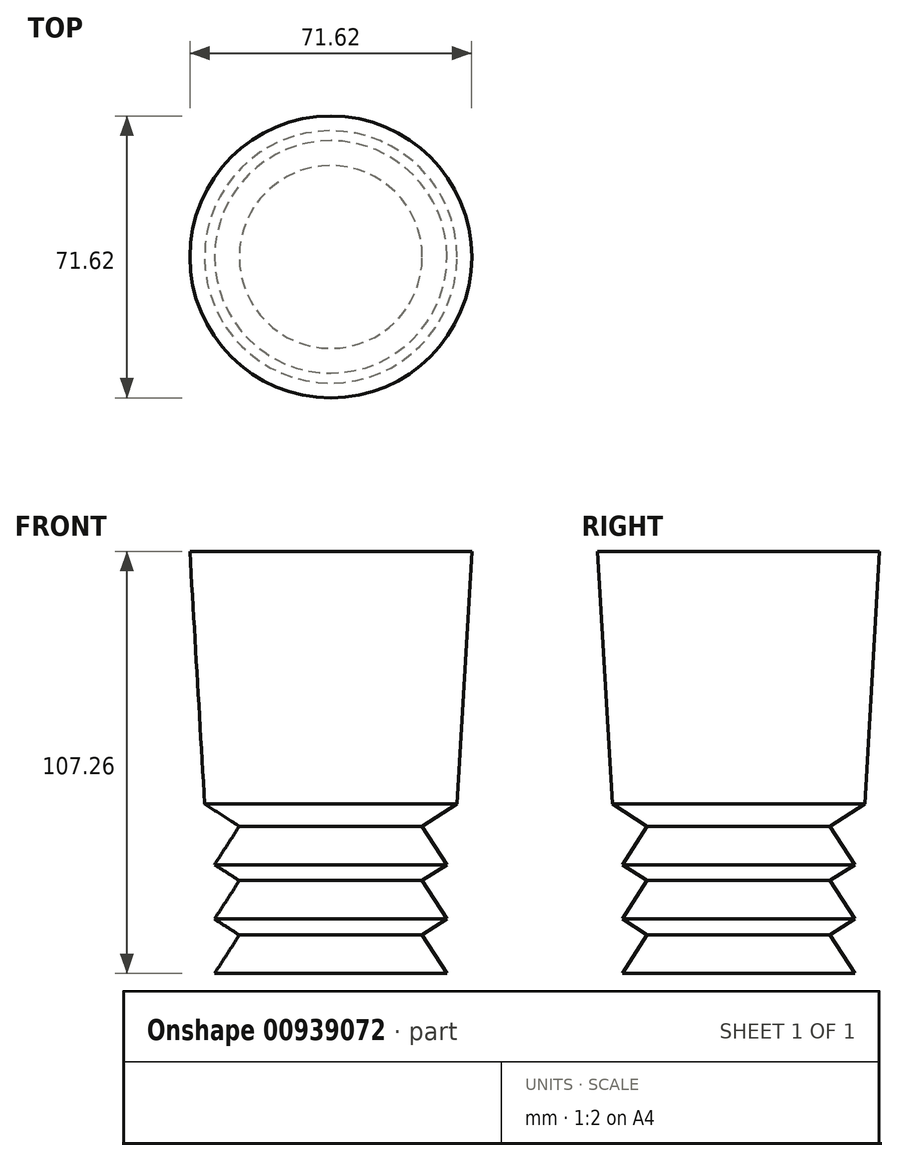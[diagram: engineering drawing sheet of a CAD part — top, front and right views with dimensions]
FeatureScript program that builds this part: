
annotation { "Feature Type Name" : "Feature", "Feature Type Description" : "" }
export const myFeature = defineFeature(function(context is Context, id is Id, definition is map)
    precondition{}
    {
        {
            var Q0;
            Q0=qCreatedBy(makeId("Front.planeOp"),FACE);
            var sketch = newSketch(context, id + "F0", { "sketchPlane" : qUnion([Q0])});
            skLineSegment(sketch, "E0", {"start": v(-35.81, 46.3) * mm, "end": v(0, 46.3) * mm});
            skLineSegment(sketch, "E1", {"start": v(0, -60.97) * mm, "end": v(-29.52, -60.97) * mm});
            skLineSegment(sketch, "E2", {"start": v(-32.05, -17.87) * mm, "end": v(-35.81, 46.3) * mm});
            skLineSegment(sketch, "E3", {"start": v(-29.52, -60.97) * mm, "end": v(-23.23, -51.19) * mm});
            skLineSegment(sketch, "E4", {"start": v(-23.23, -51.19) * mm, "end": v(-29.52, -47.14) * mm});
            skLineSegment(sketch, "E5", {"start": v(-29.52, -47.14) * mm, "end": v(-23.23, -37.36) * mm});
            skLineSegment(sketch, "E6", {"start": v(-23.23, -37.36) * mm, "end": v(-29.52, -33.32) * mm});
            skLineSegment(sketch, "E7", {"start": v(-29.52, -33.32) * mm, "end": v(-23.23, -23.53) * mm});
            skLineSegment(sketch, "E8", {"start": v(-23.23, -23.53) * mm, "end": v(-32.05, -17.87) * mm});
            skPoint(sketch, "E9.orphan", {"position": v(-29.52, -19.5) * mm});
            skLineSegment(sketch, "E10", {"start": v(0, 0) * mm, "end": v(0, 46.3) * mm});
            skLineSegment(sketch, "E11", {"start": v(0, 0) * mm, "end": v(0, -60.97) * mm});
            skSolve(sketch);
        }
        {
            var Q0;
            Q0 = qSketchRegion(id + "F0", true);
            var Q1;
            Q1=sQuery(id+"F0.wireOp",EDGE,"E10");
            revolve(context, id + "F1", {"surfaceOperationType" : NewSurfaceOperationType.NEW, "entities" : qUnion([Q0]), "axis" : qUnion([Q1]), "revolveType" : RevolveType.FULL});
        }
    });
